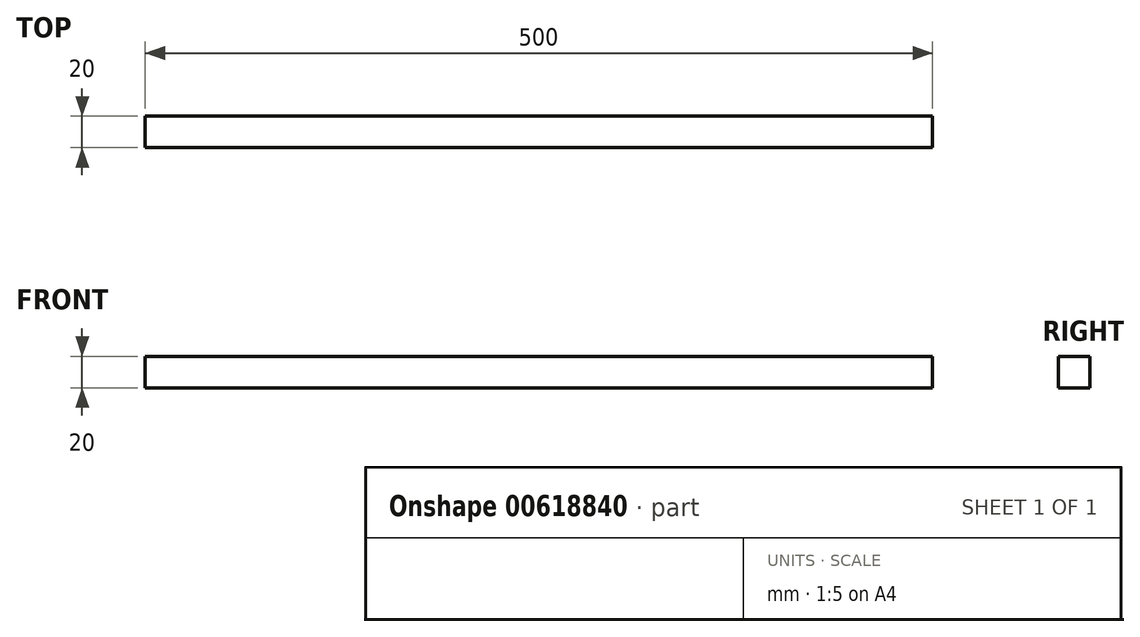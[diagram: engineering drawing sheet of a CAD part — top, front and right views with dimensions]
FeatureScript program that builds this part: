
annotation { "Feature Type Name" : "Feature", "Feature Type Description" : "" }
export const myFeature = defineFeature(function(context is Context, id is Id, definition is map)
    precondition{}
    {
        {
            var Q0;
            Q0=qCreatedBy(makeId("Top.planeOp"),FACE);
            var sketch = newSketch(context, id + "F0", { "sketchPlane" : qUnion([Q0])});
            skLineSegment(sketch, "E0.bottom", {"start": v(-250, 10) * mm, "end": v(250, 10) * mm});
            skLineSegment(sketch, "E0.top", {"start": v(-250, -10) * mm, "end": v(250, -10) * mm});
            skLineSegment(sketch, "E0.left", {"start": v(-250, 10) * mm, "end": v(-250, -10) * mm});
            skLineSegment(sketch, "E0.right", {"start": v(250, 10) * mm, "end": v(250, -10) * mm});
            skPoint(sketch, "E0.middle", {"position": v(0, 0) * mm});
            skSolve(sketch);
        }
        {
            var Q0;
            Q0 = qSketchRegion(id + "F0", true);
            extrude(context, id + "F1", {"entities" : qUnion([Q0]), "depth" : 20 * mm, "offsetDistance" : 25 * mm});
        }
    });
